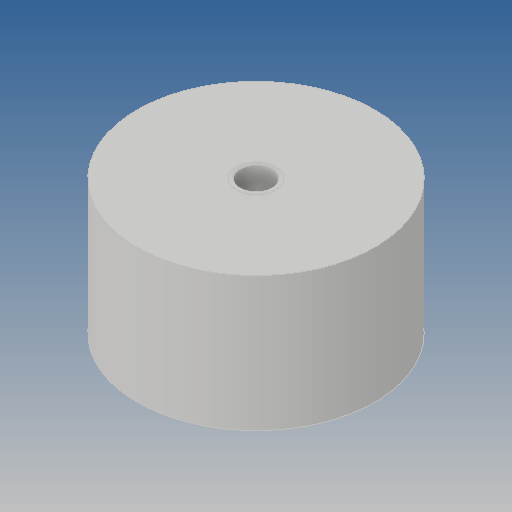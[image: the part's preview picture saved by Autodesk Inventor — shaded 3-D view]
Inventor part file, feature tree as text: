
AUTODESK INVENTOR PART (.ipt)
format: ipt  version: 2019 (Build 230136000, 136)  size: 90,624 bytes
history: native  units: mm
features: revolve x1, other x1
ambient origin geometry x8: Origin, YZ Plane, XZ Plane, XY Plane, X Axis, Y Axis, Z Axis, Center Point
bodies: Solid1 (feature_tree), Solid2 (feature_tree)
feature tree (2):
  revolve  "Revolve1"  [1 undecoded]
  other  "Boss-Extrude7"
note: 1 required parameter value undecoded (feature->parameter linkage not recoverable at this tier; creation-order binding heuristic only, values carry confidence <= 0.55)
